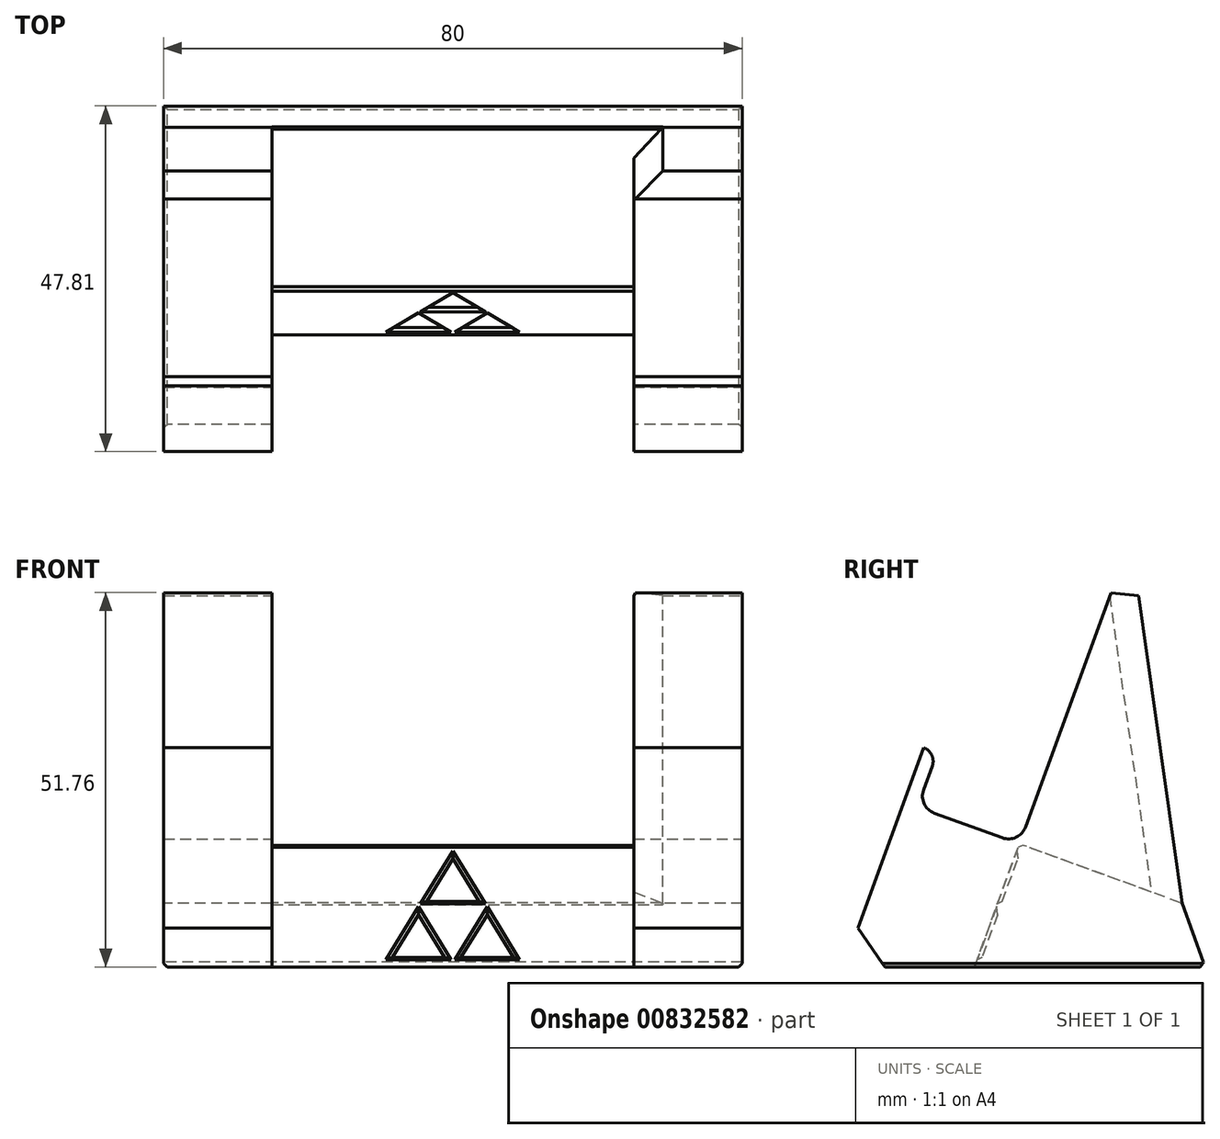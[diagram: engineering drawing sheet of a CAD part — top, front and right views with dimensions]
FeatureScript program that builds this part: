
annotation { "Feature Type Name" : "Feature", "Feature Type Description" : "" }
export const myFeature = defineFeature(function(context is Context, id is Id, definition is map)
    precondition{}
    {
        {
            var Q0;
            Q0=qCreatedBy(makeId("Top.planeOp"),FACE);
            var sketch = newSketch(context, id + "F0", { "sketchPlane" : qUnion([Q0])});
            skLineSegment(sketch, "E0.bottom", {"start": v(0, 0) * mm, "end": v(80, 0) * mm});
            skLineSegment(sketch, "E0.top", {"start": v(0, 50) * mm, "end": v(80, 50) * mm});
            skLineSegment(sketch, "E0.left", {"start": v(0, 0) * mm, "end": v(0, 50) * mm});
            skLineSegment(sketch, "E0.right", {"start": v(80, 0) * mm, "end": v(80, 50) * mm});
            skSolve(sketch);
        }
        {
            var Q0;
            Q0=qSketchRegion(id+"F0",true);
            extrude(context, id + "F1", {"entities" : qUnion([Q0]), "depth" : 60 * mm, "offsetDistance" : 25 * mm});
        }
        {
            var Q0;
            Q0=makeQuery(id+"F1.opExtrude","SWEPT_FACE",FACE,{"disambiguationData":[OSD([sQuery(id+"F0.wireOp",EDGE,"E0.left")])]});
            var sketch = newSketch(context, id + "F2", { "sketchPlane" : qUnion([Q0])});
            skLineSegment(sketch, "E1", {"start": v(0, 0) * mm, "end": v(-11.04, 30.33) * mm});
            skLineSegment(sketch, "E2", {"start": v(-11.04, 30.33) * mm, "end": v(-12.92, 29.65) * mm});
            skLineSegment(sketch, "E3", {"start": v(-12.92, 29.65) * mm, "end": v(-10.18, 22.13) * mm});
            skLineSegment(sketch, "E4", {"start": v(-10.18, 22.13) * mm, "end": v(-24.28, 17) * mm});
            skLineSegment(sketch, "E5", {"start": v(-24.28, 17) * mm, "end": v(-39.67, 59.29) * mm});
            skLineSegment(sketch, "E6", {"start": v(-39.67, 59.29) * mm, "end": v(-46.8, 8.8) * mm});
            skLineSegment(sketch, "E7", {"start": v(-46.8, 8.8) * mm, "end": v(-50, 0) * mm});
            skLineSegment(sketch, "E8", {"start": v(-50, 0) * mm, "end": v(0, 0) * mm});
            skLineSegment(sketch, "E9", {"start": v(-50, 0) * mm, "end": v(-50, 60) * mm});
            skLineSegment(sketch, "E10", {"start": v(-50, 60) * mm, "end": v(0, 60) * mm});
            skLineSegment(sketch, "E11", {"start": v(0, 60) * mm, "end": v(0, 0) * mm});
            skLineSegment(sketch, "E12", {"start": v(-46.8, 8.8) * mm, "end": v(-10.18, 22.13) * mm, "construction": true});
            skSolve(sketch);
        }
        {
            var Q0;
            Q0=makeQuery(id+"F2.imprint","IMPRINT",FACE,{"disambiguationData":[TD([[makeQuery(id+"F2.imprint","IMPRINT",EDGE,{"derivedFrom":sQuery(id+"F2.wireOp",EDGE,"E1")}),-1.0]])]});
            var Q1;
            Q1=makeQuery(id+"F1.opExtrude","SWEPT_FACE",FACE,{"disambiguationData":[OSD([sQuery(id+"F0.wireOp",EDGE,"E0.right")])]});
            extrude(context, id + "F3", {"entities" : qUnion([Q0]), "operationType" : NewBodyOperationType.REMOVE, "endBound" : BoundingType.UP_TO_SURFACE, "oppositeDirection" : true, "depth" : 25 * mm, "endBoundEntityFace" : qUnion([Q1]), "offsetDistance" : 25 * mm});
        }
        {
            var Q0;
            Q0=makeQuery(id+"F3.boolean.opBoolean","COPY",FACE,{"derivedFrom":makeQuery(id+"F3.opExtrude","SWEPT_FACE",FACE,{"disambiguationData":[OSD([sQuery(id+"F2.wireOp",EDGE,"E5")])]})});
            var sketch = newSketch(context, id + "F4", { "sketchPlane" : qUnion([Q0])});
            skLineSegment(sketch, "E13", {"start": v(15, 69.28) * mm, "end": v(65, 69.28) * mm});
            skLineSegment(sketch, "E14", {"start": v(65, 69.28) * mm, "end": v(65, 24.28) * mm});
            skLineSegment(sketch, "E15", {"start": v(65, 24.28) * mm, "end": v(15, 24.28) * mm});
            skLineSegment(sketch, "E16", {"start": v(15, 24.28) * mm, "end": v(15, 69.28) * mm});
            skSolve(sketch);
        }
        {
            var Q0;
            Q0=qSketchRegion(id+"F4",true);
            extrude(context, id + "F5", {"entities" : qUnion([Q0]), "operationType" : NewBodyOperationType.REMOVE, "endBound" : BoundingType.UP_TO_NEXT, "oppositeDirection" : true, "depth" : 25 * mm, "offsetDistance" : 25 * mm});
        }
        {
            var Q0;
            Q0=makeQuery(id+"F5.boolean.opBoolean","MERGE",FACE,{"derivedFrom":[makeQuery(id+"F3.boolean.opBoolean","COPY",FACE,{"derivedFrom":makeQuery(id+"F3.opExtrude","SWEPT_FACE",FACE,{"disambiguationData":[OSD([sQuery(id+"F2.wireOp",EDGE,"E4")])]})})],"fromTools":[makeQuery(id+"F5.opExtrude","SWEPT_FACE",FACE,{"disambiguationData":[OSD([sQuery(id+"F4.wireOp",EDGE,"E15")])]})]});
            var sketch = newSketch(context, id + "F6", { "sketchPlane" : qUnion([Q0])});
            skLineSegment(sketch, "E17", {"start": v(15, 17) * mm, "end": v(15, 0) * mm});
            skLineSegment(sketch, "E18", {"start": v(15, 17) * mm, "end": v(65, 17) * mm});
            skLineSegment(sketch, "E19", {"start": v(65, 17) * mm, "end": v(65, 0) * mm});
            skLineSegment(sketch, "E20", {"start": v(65, 0) * mm, "end": v(15, 0) * mm});
            skSolve(sketch);
        }
        {
            var Q0;
            Q0=qSketchRegion(id+"F6",true);
            var Q1;
            Q1=makeQuery(id+"F1.opExtrude","CAP_FACE",FACE,{"disambiguationData":[OSD([sQuery(id+"F0.wireOp",EDGE,"E0.bottom"),sQuery(id+"F0.wireOp",EDGE,"E0.top"),sQuery(id+"F0.wireOp",EDGE,"E0.left"),sQuery(id+"F0.wireOp",EDGE,"E0.right")])],"isStart":true});
            var Q2;
            Q2=makeQuery(id+"F3.boolean.opBoolean","COPY",FACE,{"derivedFrom":makeQuery(id+"F3.opExtrude","SWEPT_FACE",FACE,{"disambiguationData":[OSD([sQuery(id+"F2.wireOp",EDGE,"E2")])]})});
            extrude(context, id + "F7", {"entities" : qUnion([Q0]), "operationType" : NewBodyOperationType.REMOVE, "endBound" : BoundingType.UP_TO_SURFACE, "oppositeDirection" : true, "depth" : 25 * mm, "endBoundEntityFace" : qUnion([Q1]), "offsetDistance" : 25 * mm, "hasSecondDirection" : true, "secondDirectionBound" : SecondDirectionBoundingType.UP_TO_SURFACE, "secondDirectionOppositeDirection" : false, "secondDirectionDepth" : 25 * mm, "secondDirectionBoundEntityFace" : qUnion([Q2])});
        }
        {
            var Q0;
            Q0=makeQuery(id+"F7.boolean.opBoolean","COPY",FACE,{"derivedFrom":makeQuery(id+"F7.opExtrude","SWEPT_FACE",FACE,{"disambiguationData":[OSD([sQuery(id+"F6.wireOp",EDGE,"E18")])]})});
            var sketch = newSketch(context, id + "F8", { "sketchPlane" : qUnion([Q0])});
            skLineSegment(sketch, "E21", {"start": v(40, 23.28) * mm, "end": v(40, 24.28) * mm, "construction": true});
            skLineSegment(sketch, "E22", {"start": v(40, 23.28) * mm, "end": v(35.5, 15.48) * mm});
            skLineSegment(sketch, "E23", {"start": v(35.5, 15.48) * mm, "end": v(44.5, 15.48) * mm});
            skLineSegment(sketch, "E24", {"start": v(44.5, 15.48) * mm, "end": v(40, 23.28) * mm});
            skLineSegment(sketch, "E25", {"start": v(30.75, 7.26) * mm, "end": v(39.75, 7.26) * mm});
            skLineSegment(sketch, "E26", {"start": v(35.25, 15.05) * mm, "end": v(30.75, 7.26) * mm});
            skLineSegment(sketch, "E27", {"start": v(35.25, 15.05) * mm, "end": v(39.75, 7.26) * mm});
            skLineSegment(sketch, "E28", {"start": v(40.25, 7.26) * mm, "end": v(44.75, 15.05) * mm});
            skLineSegment(sketch, "E29", {"start": v(44.75, 15.05) * mm, "end": v(49.25, 7.26) * mm});
            skLineSegment(sketch, "E30", {"start": v(49.25, 7.26) * mm, "end": v(40.25, 7.26) * mm});
            skLineSegment(sketch, "E31", {"start": v(30.75, 7.26) * mm, "end": v(40, 23.28) * mm, "construction": true});
            skLineSegment(sketch, "E32", {"start": v(40, 23.28) * mm, "end": v(49.25, 7.26) * mm, "construction": true});
            skSolve(sketch);
        }
        {
            var Q0;
            Q0=qSketchRegion(id+"F8",true);
            extrude(context, id + "F9", {"entities" : qUnion([Q0]), "operationType" : NewBodyOperationType.REMOVE, "oppositeDirection" : true, "depth" : 0.5 * mm, "offsetDistance" : 25 * mm});
        }
        {
            var Q0;
            Q0=makeQuery(id+"F9.boolean.opBoolean","COPY",EDGE,{"derivedFrom":makeQuery(id+"F9.opExtrude","CAP_EDGE",EDGE,{"disambiguationData":[OSD([sQuery(id+"F8.wireOp",EDGE,"E22")])],"isStart":false})});
            var Q1;
            Q1=makeQuery(id+"F9.boolean.opBoolean","COPY",EDGE,{"derivedFrom":makeQuery(id+"F9.opExtrude","CAP_EDGE",EDGE,{"disambiguationData":[OSD([sQuery(id+"F8.wireOp",EDGE,"E24")])],"isStart":false})});
            var Q2;
            Q2=makeQuery(id+"F9.boolean.opBoolean","COPY",EDGE,{"derivedFrom":makeQuery(id+"F9.opExtrude","CAP_EDGE",EDGE,{"disambiguationData":[OSD([sQuery(id+"F8.wireOp",EDGE,"E23")])],"isStart":false})});
            var Q3;
            Q3=makeQuery(id+"F9.boolean.opBoolean","COPY",EDGE,{"derivedFrom":makeQuery(id+"F9.opExtrude","CAP_EDGE",EDGE,{"disambiguationData":[OSD([sQuery(id+"F8.wireOp",EDGE,"E27")])],"isStart":false})});
            var Q4;
            Q4=makeQuery(id+"F9.boolean.opBoolean","COPY",EDGE,{"derivedFrom":makeQuery(id+"F9.opExtrude","CAP_EDGE",EDGE,{"disambiguationData":[OSD([sQuery(id+"F8.wireOp",EDGE,"E28")])],"isStart":false})});
            var Q5;
            Q5=makeQuery(id+"F9.boolean.opBoolean","COPY",EDGE,{"derivedFrom":makeQuery(id+"F9.opExtrude","CAP_EDGE",EDGE,{"disambiguationData":[OSD([sQuery(id+"F8.wireOp",EDGE,"E26")])],"isStart":false})});
            var Q6;
            Q6=makeQuery(id+"F9.boolean.opBoolean","COPY",EDGE,{"derivedFrom":makeQuery(id+"F9.opExtrude","CAP_EDGE",EDGE,{"disambiguationData":[OSD([sQuery(id+"F8.wireOp",EDGE,"E25")])],"isStart":false})});
            var Q7;
            Q7=makeQuery(id+"F9.boolean.opBoolean","COPY",EDGE,{"derivedFrom":makeQuery(id+"F9.opExtrude","CAP_EDGE",EDGE,{"disambiguationData":[OSD([sQuery(id+"F8.wireOp",EDGE,"E30")])],"isStart":false})});
            var Q8;
            Q8=makeQuery(id+"F9.boolean.opBoolean","COPY",EDGE,{"derivedFrom":makeQuery(id+"F9.opExtrude","CAP_EDGE",EDGE,{"disambiguationData":[OSD([sQuery(id+"F8.wireOp",EDGE,"E29")])],"isStart":false})});
            chamfer(context, id + "F10", {"entities" : qUnion([Q0, Q1, Q2, Q3, Q4, Q5, Q6, Q7, Q8]), "width" : 0.5 * mm, "tangentPropagation" : true});
        }
        {
            var Q0;
            {var subQ0=sQuery(id+"F2.wireOp",EDGE,"E5");var subQ1=sQuery(id+"F2.wireOp",EDGE,"E4");Q0=makeQuery(id+"F5.boolean.opBoolean","SPLIT",EDGE,{"disambiguationData":[TD([makeQuery(id+"F1.opExtrude","SWEPT_FACE",FACE,{"disambiguationData":[OSD([sQuery(id+"F0.wireOp",EDGE,"E0.left")])]})])],"derivedFrom":makeQuery(id+"F3.boolean.opBoolean","COPY",EDGE,{"derivedFrom":makeQuery(id+"F3.opExtrude","SWEPT_EDGE",EDGE,{"disambiguationData":[OSD([subQ1,subQ0])]})})});}
            var Q1;
            {var subQ0=sQuery(id+"F2.wireOp",EDGE,"E3");var subQ1=sQuery(id+"F2.wireOp",EDGE,"E4");Q1=makeQuery(id+"F7.boolean.opBoolean","SPLIT",EDGE,{"disambiguationData":[TD([makeQuery(id+"F1.opExtrude","SWEPT_FACE",FACE,{"disambiguationData":[OSD([sQuery(id+"F0.wireOp",EDGE,"E0.left")])]})])],"derivedFrom":makeQuery(id+"F3.boolean.opBoolean","COPY",EDGE,{"derivedFrom":makeQuery(id+"F3.opExtrude","SWEPT_EDGE",EDGE,{"disambiguationData":[OSD([subQ0,subQ1])]})})});}
            var Q2;
            {var subQ0=sQuery(id+"F2.wireOp",EDGE,"E4");var subQ1=sQuery(id+"F2.wireOp",EDGE,"E5");Q2=makeQuery(id+"F5.boolean.opBoolean","SPLIT",EDGE,{"disambiguationData":[TD([makeQuery(id+"F1.opExtrude","SWEPT_FACE",FACE,{"disambiguationData":[OSD([sQuery(id+"F0.wireOp",EDGE,"E0.right")])]})])],"derivedFrom":makeQuery(id+"F3.boolean.opBoolean","COPY",EDGE,{"derivedFrom":makeQuery(id+"F3.opExtrude","SWEPT_EDGE",EDGE,{"disambiguationData":[OSD([subQ0,subQ1])]})})});}
            var Q3;
            {var subQ0=sQuery(id+"F2.wireOp",EDGE,"E3");var subQ1=sQuery(id+"F2.wireOp",EDGE,"E4");Q3=makeQuery(id+"F7.boolean.opBoolean","SPLIT",EDGE,{"disambiguationData":[TD([makeQuery(id+"F1.opExtrude","SWEPT_FACE",FACE,{"disambiguationData":[OSD([sQuery(id+"F0.wireOp",EDGE,"E0.right")])]})])],"derivedFrom":makeQuery(id+"F3.boolean.opBoolean","COPY",EDGE,{"derivedFrom":makeQuery(id+"F3.opExtrude","SWEPT_EDGE",EDGE,{"disambiguationData":[OSD([subQ0,subQ1])]})})});}
            fillet(context, id + "F11", {"entities" : qUnion([Q0, Q1, Q2, Q3]), "radius" : 2.5 * mm, "tangentPropagation" : true, "allowEdgeOverflow" : false});
        }
        {
            var Q0;
            {var subQ0=sQuery(id+"F2.wireOp",EDGE,"E2");var subQ1=sQuery(id+"F2.wireOp",EDGE,"E3");Q0=makeQuery(id+"F7.boolean.opBoolean","SPLIT",EDGE,{"disambiguationData":[TD([makeQuery(id+"F1.opExtrude","SWEPT_FACE",FACE,{"disambiguationData":[OSD([sQuery(id+"F0.wireOp",EDGE,"E0.left")])]})])],"derivedFrom":makeQuery(id+"F3.boolean.opBoolean","COPY",EDGE,{"derivedFrom":makeQuery(id+"F3.opExtrude","SWEPT_EDGE",EDGE,{"disambiguationData":[OSD([subQ0,subQ1])]})})});}
            var Q1;
            {var subQ0=sQuery(id+"F2.wireOp",EDGE,"E2");var subQ1=sQuery(id+"F2.wireOp",EDGE,"E3");Q1=makeQuery(id+"F7.boolean.opBoolean","SPLIT",EDGE,{"disambiguationData":[TD([makeQuery(id+"F1.opExtrude","SWEPT_FACE",FACE,{"disambiguationData":[OSD([sQuery(id+"F0.wireOp",EDGE,"E0.right")])]})])],"derivedFrom":makeQuery(id+"F3.boolean.opBoolean","COPY",EDGE,{"derivedFrom":makeQuery(id+"F3.opExtrude","SWEPT_EDGE",EDGE,{"disambiguationData":[OSD([subQ0,subQ1])]})})});}
            fillet(context, id + "F12", {"entities" : qUnion([Q0, Q1]), "radius" : 2 * mm, "tangentPropagation" : true, "allowEdgeOverflow" : false});
        }
        {
            var Q0;
            {var subQ0=sQuery(id+"F2.wireOp",EDGE,"E6");var subQ1=sQuery(id+"F2.wireOp",EDGE,"E5");Q0=makeQuery(id+"F5.boolean.opBoolean","SPLIT",EDGE,{"disambiguationData":[TD([makeQuery(id+"F1.opExtrude","SWEPT_FACE",FACE,{"disambiguationData":[OSD([sQuery(id+"F0.wireOp",EDGE,"E0.left")])]})])],"derivedFrom":makeQuery(id+"F3.boolean.opBoolean","COPY",EDGE,{"derivedFrom":makeQuery(id+"F3.opExtrude","SWEPT_EDGE",EDGE,{"disambiguationData":[OSD([subQ1,subQ0])]})})});}
            var Q1;
            {var subQ0=sQuery(id+"F2.wireOp",EDGE,"E5");var subQ1=sQuery(id+"F2.wireOp",EDGE,"E6");Q1=makeQuery(id+"F5.boolean.opBoolean","SPLIT",EDGE,{"disambiguationData":[TD([makeQuery(id+"F1.opExtrude","SWEPT_FACE",FACE,{"disambiguationData":[OSD([sQuery(id+"F0.wireOp",EDGE,"E0.right")])]})])],"derivedFrom":makeQuery(id+"F3.boolean.opBoolean","COPY",EDGE,{"derivedFrom":makeQuery(id+"F3.opExtrude","SWEPT_EDGE",EDGE,{"disambiguationData":[OSD([subQ0,subQ1])]})})});}
            chamfer(context, id + "F13", {"entities" : qUnion([Q0, Q1]), "width" : 2 * mm, "tangentPropagation" : true});
        }
        {
            var Q0;
            Q0=makeQuery(id+"F3.boolean.opBoolean","COPY",EDGE,{"derivedFrom":makeQuery(id+"F3.opExtrude","CAP_EDGE",EDGE,{"disambiguationData":[OSD([sQuery(id+"F2.wireOp",EDGE,"E1")])],"isStart":true})});
            var Q1;
            {var subQ0=sQuery(id+"F6.wireOp",EDGE,"E20");var subQ1=sQuery(id+"F6.wireOp",EDGE,"E17");var subQ2=sQuery(id+"F2.wireOp",EDGE,"E4");var subQ3=makeQuery(id+"F6.imprint","INTERSECT",VERTEX,{"derivedFrom":[makeQuery(id+"F3.boolean.opBoolean","COPY",EDGE,{"derivedFrom":makeQuery(id+"F3.opExtrude","SWEPT_EDGE",EDGE,{"disambiguationData":[OSD([sQuery(id+"F2.wireOp",EDGE,"E3"),subQ2])]})}),subQ1]});Q1=makeQuery(id+"F7.boolean.opBoolean","COPY",EDGE,{"derivedFrom":makeQuery(id+"F7.opExtrude","TWEAK_EDGE",EDGE,{"derivedFrom":[makeQuery(id+"F6.imprint","IMPRINT",EDGE,{"disambiguationData":[TD([[subQ3,1.0]])],"derivedFrom":subQ1}),makeQuery(id+"F6.imprint","IMPRINT",EDGE,{"disambiguationData":[TD([[makeQuery(id+"F6.imprint","INTERSECT",VERTEX,{"derivedFrom":[subQ1,subQ0]}),1.0]])],"derivedFrom":subQ1}),makeQuery(id+"F6.imprint","IMPRINT",EDGE,{"derivedFrom":subQ0})]})});}
            var Q2;
            {var subQ0=sQuery(id+"F6.wireOp",EDGE,"E20");var subQ1=sQuery(id+"F6.wireOp",EDGE,"E19");var subQ2=sQuery(id+"F2.wireOp",EDGE,"E4");var subQ3=makeQuery(id+"F6.imprint","INTERSECT",VERTEX,{"derivedFrom":[makeQuery(id+"F3.boolean.opBoolean","COPY",EDGE,{"derivedFrom":makeQuery(id+"F3.opExtrude","SWEPT_EDGE",EDGE,{"disambiguationData":[OSD([sQuery(id+"F2.wireOp",EDGE,"E3"),subQ2])]})}),subQ1]});Q2=makeQuery(id+"F7.boolean.opBoolean","COPY",EDGE,{"derivedFrom":makeQuery(id+"F7.opExtrude","TWEAK_EDGE",EDGE,{"derivedFrom":[makeQuery(id+"F6.imprint","IMPRINT",EDGE,{"disambiguationData":[TD([[subQ3,1.0]])],"derivedFrom":subQ1}),makeQuery(id+"F6.imprint","IMPRINT",EDGE,{"disambiguationData":[TD([[makeQuery(id+"F6.imprint","INTERSECT",VERTEX,{"derivedFrom":[subQ1,subQ0]}),1.0]])],"derivedFrom":subQ1}),makeQuery(id+"F6.imprint","IMPRINT",EDGE,{"derivedFrom":subQ0})]})});}
            var Q3;
            Q3=makeQuery(id+"F3.boolean.opBoolean","COPY",EDGE,{"derivedFrom":makeQuery(id+"F3.opExtrude","CAP_EDGE",EDGE,{"disambiguationData":[OSD([sQuery(id+"F2.wireOp",EDGE,"E1")])],"isStart":false})});
            var Q4;
            {var subQ0=sQuery(id+"F0.wireOp",EDGE,"E0.left");var subQ1=sQuery(id+"F0.wireOp",EDGE,"E0.bottom");var subQ2=sQuery(id+"F2.wireOp",EDGE,"E1");Q4=makeQuery(id+"F7.boolean.opBoolean","SPLIT",EDGE,{"disambiguationData":[TD([makeQuery(id+"F1.opExtrude","SWEPT_FACE",FACE,{"disambiguationData":[OSD([subQ0])]})])],"derivedFrom":makeQuery(id+"F3.boolean.opBoolean","MERGE",EDGE,{"derivedFrom":[makeQuery(id+"F1.opExtrude","CAP_EDGE",EDGE,{"disambiguationData":[OSD([subQ1])],"isStart":true})],"fromTools":[makeQuery(id+"F3.opExtrude","SWEPT_EDGE",EDGE,{"disambiguationData":[OSD([subQ2,sQuery(id+"F2.wireOp",EDGE,"E8"),sQuery(id+"F2.wireOp",EDGE,"E11")])]})]})});}
            var Q5;
            {var subQ0=sQuery(id+"F0.wireOp",EDGE,"E0.right");var subQ1=sQuery(id+"F0.wireOp",EDGE,"E0.bottom");var subQ2=sQuery(id+"F2.wireOp",EDGE,"E1");Q5=makeQuery(id+"F7.boolean.opBoolean","SPLIT",EDGE,{"disambiguationData":[TD([makeQuery(id+"F1.opExtrude","SWEPT_FACE",FACE,{"disambiguationData":[OSD([subQ0])]})])],"derivedFrom":makeQuery(id+"F3.boolean.opBoolean","MERGE",EDGE,{"derivedFrom":[makeQuery(id+"F1.opExtrude","CAP_EDGE",EDGE,{"disambiguationData":[OSD([subQ1])],"isStart":true})],"fromTools":[makeQuery(id+"F3.opExtrude","SWEPT_EDGE",EDGE,{"disambiguationData":[OSD([subQ2,sQuery(id+"F2.wireOp",EDGE,"E8"),sQuery(id+"F2.wireOp",EDGE,"E11")])]})]})});}
            var Q6;
            Q6=makeQuery(id+"F3.boolean.opBoolean","COPY",EDGE,{"derivedFrom":makeQuery(id+"F3.opExtrude","CAP_EDGE",EDGE,{"disambiguationData":[OSD([sQuery(id+"F2.wireOp",EDGE,"E6")])],"isStart":false})});
            var Q7;
            Q7=makeQuery(id+"F3.boolean.opBoolean","COPY",EDGE,{"derivedFrom":makeQuery(id+"F3.opExtrude","CAP_EDGE",EDGE,{"disambiguationData":[OSD([sQuery(id+"F2.wireOp",EDGE,"E7")])],"isStart":false})});
            var Q8;
            Q8=makeQuery(id+"F3.boolean.opBoolean","COPY",EDGE,{"derivedFrom":makeQuery(id+"F3.opExtrude","CAP_EDGE",EDGE,{"disambiguationData":[OSD([sQuery(id+"F2.wireOp",EDGE,"E7")])],"isStart":true})});
            var Q9;
            Q9=makeQuery(id+"F3.boolean.opBoolean","COPY",EDGE,{"derivedFrom":makeQuery(id+"F3.opExtrude","CAP_EDGE",EDGE,{"disambiguationData":[OSD([sQuery(id+"F2.wireOp",EDGE,"E6")])],"isStart":true})});
            var Q10;
            Q10=makeQuery(id+"F5.boolean.opBoolean","COPY",EDGE,{"derivedFrom":makeQuery(id+"F5.opExtrude","TWEAK_EDGE",EDGE,{"derivedFrom":[makeQuery(id+"F3.boolean.opBoolean","COPY",FACE,{"derivedFrom":makeQuery(id+"F3.opExtrude","SWEPT_FACE",FACE,{"disambiguationData":[OSD([sQuery(id+"F2.wireOp",EDGE,"E6")])]})}),makeQuery(id+"F4.imprint","IMPRINT",EDGE,{"derivedFrom":sQuery(id+"F4.wireOp",EDGE,"E16")})]})});
            var Q11;
            Q11=makeQuery(id+"F5.boolean.opBoolean","COPY",EDGE,{"derivedFrom":makeQuery(id+"F5.opExtrude","TWEAK_EDGE",EDGE,{"derivedFrom":[makeQuery(id+"F3.boolean.opBoolean","COPY",FACE,{"derivedFrom":makeQuery(id+"F3.opExtrude","SWEPT_FACE",FACE,{"disambiguationData":[OSD([sQuery(id+"F2.wireOp",EDGE,"E6")])]})}),makeQuery(id+"F4.imprint","IMPRINT",EDGE,{"derivedFrom":sQuery(id+"F4.wireOp",EDGE,"E14")})]})});
            chamfer(context, id + "F14", {"entities" : qUnion([Q0, Q1, Q2, Q3, Q4, Q5, Q6, Q7, Q8, Q9, Q10, Q11]), "width" : 4 * mm, "tangentPropagation" : true});
        }
        {
            var Q0;
            Q0=makeQuery(id+"F1.opExtrude","CAP_EDGE",EDGE,{"disambiguationData":[OSD([sQuery(id+"F0.wireOp",EDGE,"E0.right")])],"isStart":true});
            var Q1;
            Q1=makeQuery(id+"F14.opChamfer","BLEND_EDGE",EDGE,{"blendedFrom":[makeQuery(id+"F3.boolean.opBoolean","COPY",EDGE,{"derivedFrom":makeQuery(id+"F3.opExtrude","CAP_EDGE",EDGE,{"disambiguationData":[OSD([sQuery(id+"F2.wireOp",EDGE,"E7")])],"isStart":false})}),makeQuery(id+"F1.opExtrude","CAP_FACE",FACE,{"disambiguationData":[OSD([sQuery(id+"F0.wireOp",EDGE,"E0.bottom"),sQuery(id+"F0.wireOp",EDGE,"E0.top"),sQuery(id+"F0.wireOp",EDGE,"E0.left"),sQuery(id+"F0.wireOp",EDGE,"E0.right")])],"isStart":true})],"blendedInto":[makeQuery(id+"F1.opExtrude","CAP_FACE",FACE,{"disambiguationData":[OSD([sQuery(id+"F0.wireOp",EDGE,"E0.bottom"),sQuery(id+"F0.wireOp",EDGE,"E0.top"),sQuery(id+"F0.wireOp",EDGE,"E0.left"),sQuery(id+"F0.wireOp",EDGE,"E0.right")])],"isStart":true})]});
            var Q2;
            Q2=makeQuery(id+"F3.boolean.opBoolean","MERGE",EDGE,{"derivedFrom":[makeQuery(id+"F1.opExtrude","CAP_EDGE",EDGE,{"disambiguationData":[OSD([sQuery(id+"F0.wireOp",EDGE,"E0.top")])],"isStart":true})],"fromTools":[makeQuery(id+"F3.opExtrude","SWEPT_EDGE",EDGE,{"disambiguationData":[OSD([sQuery(id+"F2.wireOp",EDGE,"E7"),sQuery(id+"F2.wireOp",EDGE,"E8"),sQuery(id+"F2.wireOp",EDGE,"E9")])]})]});
            var Q3;
            Q3=makeQuery(id+"F14.opChamfer","BLEND_EDGE",EDGE,{"blendedFrom":[makeQuery(id+"F3.boolean.opBoolean","COPY",EDGE,{"derivedFrom":makeQuery(id+"F3.opExtrude","CAP_EDGE",EDGE,{"disambiguationData":[OSD([sQuery(id+"F2.wireOp",EDGE,"E7")])],"isStart":true})}),makeQuery(id+"F1.opExtrude","CAP_FACE",FACE,{"disambiguationData":[OSD([sQuery(id+"F0.wireOp",EDGE,"E0.bottom"),sQuery(id+"F0.wireOp",EDGE,"E0.top"),sQuery(id+"F0.wireOp",EDGE,"E0.left"),sQuery(id+"F0.wireOp",EDGE,"E0.right")])],"isStart":true})],"blendedInto":[makeQuery(id+"F1.opExtrude","CAP_FACE",FACE,{"disambiguationData":[OSD([sQuery(id+"F0.wireOp",EDGE,"E0.bottom"),sQuery(id+"F0.wireOp",EDGE,"E0.top"),sQuery(id+"F0.wireOp",EDGE,"E0.left"),sQuery(id+"F0.wireOp",EDGE,"E0.right")])],"isStart":true})]});
            var Q4;
            Q4=makeQuery(id+"F1.opExtrude","CAP_EDGE",EDGE,{"disambiguationData":[OSD([sQuery(id+"F0.wireOp",EDGE,"E0.left")])],"isStart":true});
            var Q5;
            Q5=makeQuery(id+"F7.boolean.opBoolean","COPY",EDGE,{"derivedFrom":makeQuery(id+"F7.opExtrude","CAP_EDGE",EDGE,{"disambiguationData":[OSD([sQuery(id+"F6.wireOp",EDGE,"E19")])],"isStart":false})});
            var Q6;
            Q6=makeQuery(id+"F7.boolean.opBoolean","COPY",EDGE,{"derivedFrom":makeQuery(id+"F7.opExtrude","CAP_EDGE",EDGE,{"disambiguationData":[OSD([sQuery(id+"F6.wireOp",EDGE,"E17")])],"isStart":false})});
            var Q7;
            Q7=makeQuery(id+"F7.boolean.opBoolean","INTERSECT",EDGE,{"derivedFrom":[makeQuery(id+"F5.boolean.opBoolean","MERGE",FACE,{"derivedFrom":[makeQuery(id+"F3.boolean.opBoolean","COPY",FACE,{"derivedFrom":makeQuery(id+"F3.opExtrude","SWEPT_FACE",FACE,{"disambiguationData":[OSD([sQuery(id+"F2.wireOp",EDGE,"E4")])]})})],"fromTools":[makeQuery(id+"F5.opExtrude","SWEPT_FACE",FACE,{"disambiguationData":[OSD([sQuery(id+"F4.wireOp",EDGE,"E15")])]})]}),makeQuery(id+"F7.opExtrude","SWEPT_FACE",FACE,{"disambiguationData":[OSD([sQuery(id+"F6.wireOp",EDGE,"E18")])]})]});
            var Q8;
            Q8=makeQuery(id+"F5.boolean.opBoolean","MERGE",EDGE,{"derivedFrom":[makeQuery(id+"F3.boolean.opBoolean","COPY",EDGE,{"derivedFrom":makeQuery(id+"F3.opExtrude","SWEPT_EDGE",EDGE,{"disambiguationData":[OSD([sQuery(id+"F2.wireOp",EDGE,"E6"),sQuery(id+"F2.wireOp",EDGE,"E7")])]})})],"fromTools":[makeQuery(id+"F5.opExtrude","CAP_EDGE",EDGE,{"disambiguationData":[OSD([sQuery(id+"F4.wireOp",EDGE,"E15")])],"isStart":false})]});
            chamfer(context, id + "F15", {"entities" : qUnion([Q0, Q1, Q2, Q3, Q4, Q5, Q6, Q7, Q8]), "width" : 0.5 * mm, "tangentPropagation" : true});
        }
    });
